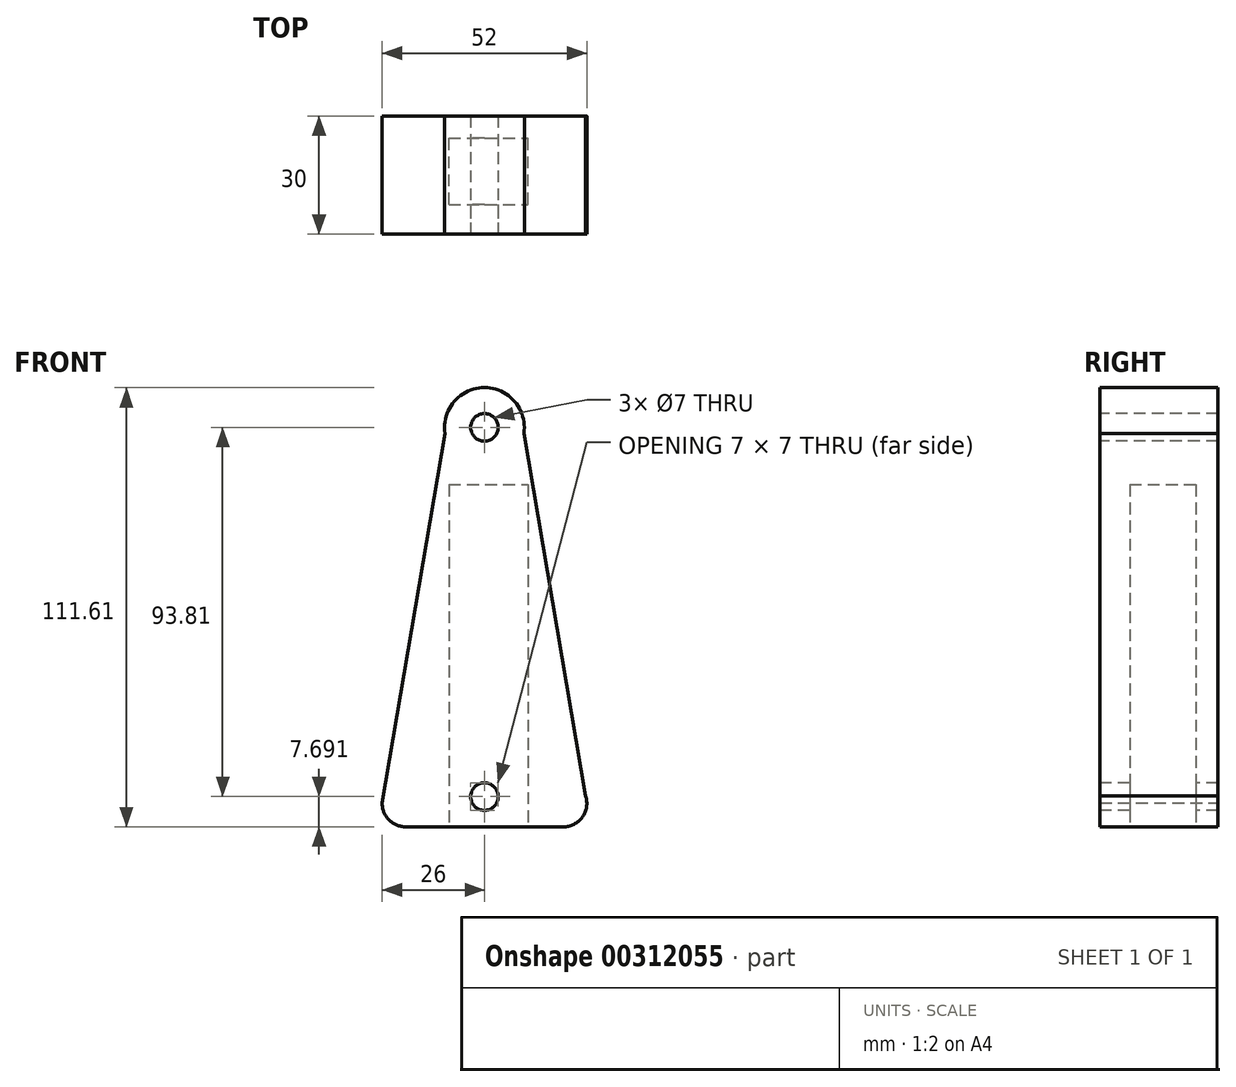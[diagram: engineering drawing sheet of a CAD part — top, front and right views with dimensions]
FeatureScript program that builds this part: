
annotation { "Feature Type Name" : "Feature", "Feature Type Description" : "" }
export const myFeature = defineFeature(function(context is Context, id is Id, definition is map)
    precondition{}
    {
        {
            var Q0;
            Q0=qCreatedBy(makeId("Front.planeOp"),FACE);
            var sketch = newSketch(context, id + "F0", { "sketchPlane" : qUnion([Q0])});
            skLineSegment(sketch, "E0", {"start": v(0, 0) * mm, "end": v(40, 0) * mm});
            skLineSegment(sketch, "E1", {"start": v(20, 0) * mm, "end": v(20, 100) * mm, "construction": true});
            skArc(sketch, "E2", {"start": v(0, 0) * mm, "mid": v(-4.3, 1.81) * mm, "end": v(-6, 6.15) * mm});
            skArc(sketch, "E3", {"start": v(40, 0) * mm, "mid": v(44.86, 2.48) * mm, "end": v(45.7, 7.87) * mm});
            skLineSegment(sketch, "E4", {"start": v(20, 100) * mm, "end": v(30, 100) * mm});
            skLineSegment(sketch, "E5", {"start": v(20, 100) * mm, "end": v(10, 100) * mm});
            skLineSegment(sketch, "E6", {"start": v(10, 100) * mm, "end": v(-6, 6.15) * mm});
            skLineSegment(sketch, "E7", {"start": v(30, 100) * mm, "end": v(45.7, 7.87) * mm});
            skArc(sketch, "E8", {"start": v(30, 100) * mm, "mid": v(20, 111.61) * mm, "end": v(10, 100) * mm});
            skSolve(sketch);
        }
        {
            var Q0;
            Q0 = qSketchRegion(id + "F0", true);
            extrude(context, id + "F1", {"entities" : qUnion([Q0]), "depth" : 30 * mm});
        }
        {
            var Q0;
            Q0=makeQuery(id+"F1.opExtrude","CAP_FACE",FACE,{"disambiguationData":[OSD([sQuery(id+"F0.wireOp",EDGE,"E0"),sQuery(id+"F0.wireOp",EDGE,"E2"),sQuery(id+"F0.wireOp",EDGE,"E3"),sQuery(id+"F0.wireOp",EDGE,"E6"),sQuery(id+"F0.wireOp",EDGE,"E7"),sQuery(id+"F0.wireOp",EDGE,"E8")])],"isStart":false});
            var sketch = newSketch(context, id + "F2", { "sketchPlane" : qUnion([Q0])});
            skCircle(sketch, "E9", {"center": v(20, 7.7) * mm, "radius": 1.78 * mm});
            skPoint(sketch, "E9.centerSnap0", {"position": v(20, 0) * mm});
            skSolve(sketch);
        }
        {
            var Q0;
            Q0=sQuery(id+"F2.wireOp",VERTEX,"E9.center");
            var Q1;
            Q1=makeQuery(id+"F1.opExtrude","SWEPT_BODY",BODY,{"disambiguationData":[OSD([sQuery(id+"F0.wireOp",EDGE,"E0"),sQuery(id+"F0.wireOp",EDGE,"E2"),sQuery(id+"F0.wireOp",EDGE,"E3"),sQuery(id+"F0.wireOp",EDGE,"E6"),sQuery(id+"F0.wireOp",EDGE,"E7"),sQuery(id+"F0.wireOp",EDGE,"E8")])]});
            hole(context, id + "F3", {"style" : HoleStyle.SIMPLE, "endStyle" : HoleEndStyle.THROUGH, "standardTappedOrClearance" : lookupTablePath({ "standard" : "ISO", "engagement" : "75%", "pitch" : "1 mm", "size" : "M8", "type" : "Tapped" }), "standardBlindInLast" : lookupTablePath({ "standard" : "ISO", "engagement" : "75%", "pitch" : "1 mm", "size" : "M8", "type" : "Tapped" }), "holeDiameter" : 7 * mm, "showTappedDepth" : true, "tappedDepth" : 6 * mm, "tapClearance" : 3, "locations" : qUnion([Q0]), "scope" : qUnion([Q1]), "majorDiameter" : 8 * mm});
        }
        {
            var Q0;
            Q0=makeQuery(id+"F1.opExtrude","CAP_FACE",FACE,{"disambiguationData":[OSD([sQuery(id+"F0.wireOp",EDGE,"E0"),sQuery(id+"F0.wireOp",EDGE,"E2"),sQuery(id+"F0.wireOp",EDGE,"E3"),sQuery(id+"F0.wireOp",EDGE,"E6"),sQuery(id+"F0.wireOp",EDGE,"E7"),sQuery(id+"F0.wireOp",EDGE,"E8")])],"isStart":false});
            var sketch = newSketch(context, id + "F4", { "sketchPlane" : qUnion([Q0])});
            skCircle(sketch, "E10", {"center": v(20, 101.5) * mm, "radius": 2.09 * mm});
            skSolve(sketch);
        }
        {
            var Q0;
            Q0=sQuery(id+"F4.wireOp",VERTEX,"E10.center");
            var Q1;
            Q1=makeQuery(id+"F1.opExtrude","SWEPT_BODY",BODY,{"disambiguationData":[OSD([sQuery(id+"F0.wireOp",EDGE,"E0"),sQuery(id+"F0.wireOp",EDGE,"E2"),sQuery(id+"F0.wireOp",EDGE,"E3"),sQuery(id+"F0.wireOp",EDGE,"E6"),sQuery(id+"F0.wireOp",EDGE,"E7"),sQuery(id+"F0.wireOp",EDGE,"E8")])]});
            hole(context, id + "F5", {"style" : HoleStyle.SIMPLE, "endStyle" : HoleEndStyle.THROUGH, "standardTappedOrClearance" : lookupTablePath({ "standard" : "ISO", "engagement" : "75%", "pitch" : "1 mm", "size" : "M8", "type" : "Tapped" }), "standardBlindInLast" : lookupTablePath({ "standard" : "ISO", "engagement" : "75%", "pitch" : "1 mm", "size" : "M8", "type" : "Tapped" }), "holeDiameter" : 7 * mm, "showTappedDepth" : true, "tappedDepth" : 6 * mm, "tapClearance" : 3, "locations" : qUnion([Q0]), "scope" : qUnion([Q1]), "majorDiameter" : 8 * mm});
        }
        {
            var Q0;
            Q0=makeQuery(id+"F1.opExtrude","SWEPT_FACE",FACE,{"disambiguationData":[OSD([sQuery(id+"F0.wireOp",EDGE,"E0")])]});
            var sketch = newSketch(context, id + "F6", { "sketchPlane" : qUnion([Q0])});
            skLineSegment(sketch, "E11.bottom", {"start": v(10.96, 22.45) * mm, "end": v(31.03, 22.45) * mm});
            skLineSegment(sketch, "E11.top", {"start": v(10.96, 5.64) * mm, "end": v(31.03, 5.64) * mm});
            skLineSegment(sketch, "E11.left", {"start": v(10.96, 22.45) * mm, "end": v(10.96, 5.64) * mm});
            skLineSegment(sketch, "E11.right", {"start": v(31.03, 22.45) * mm, "end": v(31.03, 5.64) * mm});
            skPoint(sketch, "E11.middle", {"position": v(21, 14.04) * mm});
            skSolve(sketch);
        }
        {
            var Q0;
            Q0 = qSketchRegion(id + "F6", true);
            extrude(context, id + "F7", {"entities" : qUnion([Q0]), "operationType" : NewBodyOperationType.REMOVE, "oppositeDirection" : true, "depth" : 87 * mm});
        }
    });
